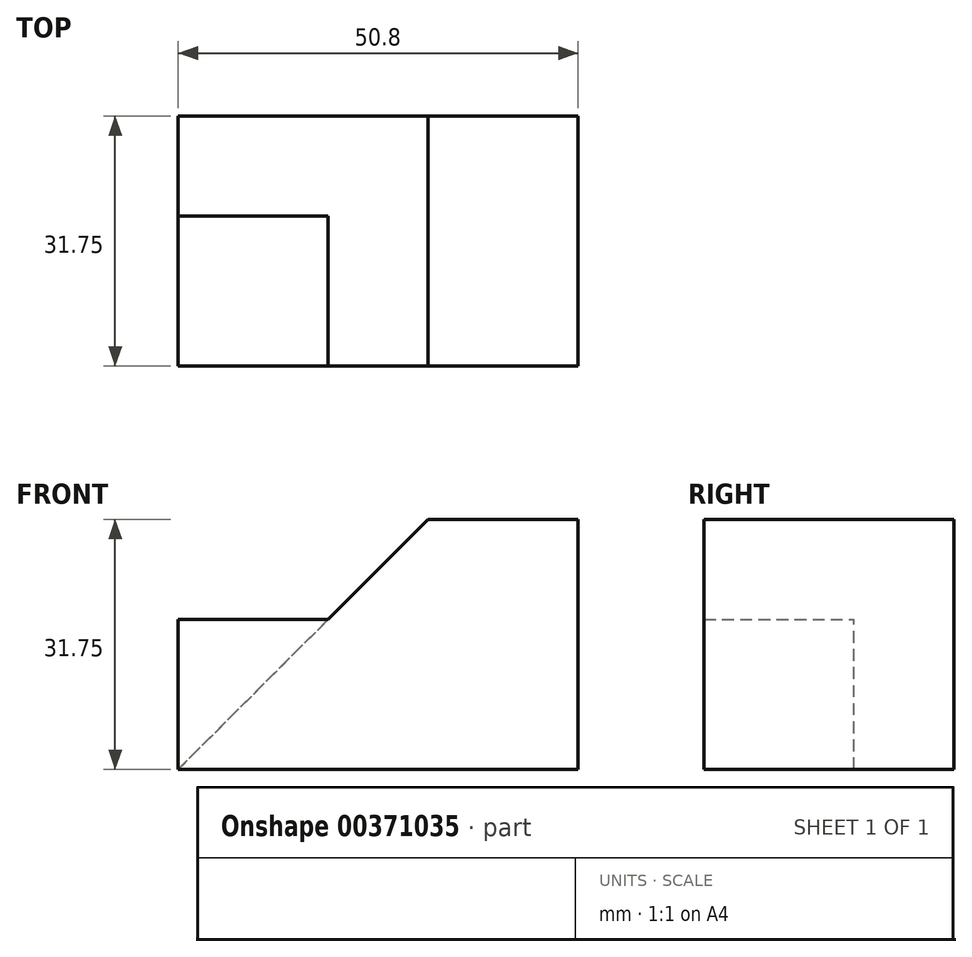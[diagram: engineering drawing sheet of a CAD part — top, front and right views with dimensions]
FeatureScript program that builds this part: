
annotation { "Feature Type Name" : "Feature", "Feature Type Description" : "" }
export const myFeature = defineFeature(function(context is Context, id is Id, definition is map)
    precondition{}
    {
        {
            var Q0;
            Q0=qCreatedBy(makeId("Front.planeOp"),FACE);
            var sketch = newSketch(context, id + "F0", { "sketchPlane" : qUnion([Q0])});
            skLineSegment(sketch, "E0", {"start": v(-48.86, 0) * mm, "end": v(-48.86, 31.75) * mm});
            skLineSegment(sketch, "E1", {"start": v(-48.86, 0) * mm, "end": v(1.94, 0) * mm});
            skLineSegment(sketch, "E2", {"start": v(1.94, 0) * mm, "end": v(1.94, 31.75) * mm});
            skLineSegment(sketch, "E3", {"start": v(-48.86, 31.75) * mm, "end": v(1.94, 31.75) * mm});
            skSolve(sketch);
        }
        {
            var Q0;
            Q0=makeQuery(id+"F0.imprint","IMPRINT",FACE,{"disambiguationData":[TD([[makeQuery(id+"F0.imprint","IMPRINT",EDGE,{"derivedFrom":sQuery(id+"F0.wireOp",EDGE,"E0")}),-1.0]])]});
            extrude(context, id + "F1", {"entities" : qUnion([Q0]), "depth" : 31.75 * mm});
        }
        {
            var Q0;
            Q0=makeQuery(id+"F1.opExtrude","CAP_FACE",FACE,{"disambiguationData":[OSD([sQuery(id+"F0.wireOp",EDGE,"E0"),sQuery(id+"F0.wireOp",EDGE,"E1"),sQuery(id+"F0.wireOp",EDGE,"E2"),sQuery(id+"F0.wireOp",EDGE,"E3")])],"isStart":true});
            var sketch = newSketch(context, id + "F2", { "sketchPlane" : qUnion([Q0])});
            skLineSegment(sketch, "E4", {"start": v(48.86, 0) * mm, "end": v(48.86, 19.05) * mm});
            skLineSegment(sketch, "E5", {"start": v(48.86, 19.05) * mm, "end": v(29.81, 19.05) * mm});
            skLineSegment(sketch, "E6", {"start": v(-1.94, 31.75) * mm, "end": v(17.11, 31.75) * mm});
            skLineSegment(sketch, "E7", {"start": v(17.11, 31.75) * mm, "end": v(29.81, 19.05) * mm});
            skLineSegment(sketch, "E8", {"start": v(17.11, 31.75) * mm, "end": v(48.86, 31.75) * mm});
            skLineSegment(sketch, "E9", {"start": v(48.86, 31.75) * mm, "end": v(48.86, 19.05) * mm});
            skSolve(sketch);
        }
        {
            var Q0;
            Q0=makeQuery(id+"F2.imprint","IMPRINT",FACE,{"disambiguationData":[TD([[makeQuery(id+"F2.imprint","IMPRINT",EDGE,{"derivedFrom":sQuery(id+"F2.wireOp",EDGE,"E5")}),-1.0]])]});
            extrude(context, id + "F3", {"entities" : qUnion([Q0]), "operationType" : NewBodyOperationType.REMOVE, "oppositeDirection" : true, "depth" : 38.1 * mm});
        }
        {
            var Q0;
            Q0=makeQuery(id+"F1.opExtrude","CAP_FACE",FACE,{"disambiguationData":[OSD([sQuery(id+"F0.wireOp",EDGE,"E0"),sQuery(id+"F0.wireOp",EDGE,"E1"),sQuery(id+"F0.wireOp",EDGE,"E2"),sQuery(id+"F0.wireOp",EDGE,"E3")])],"isStart":true});
            var sketch = newSketch(context, id + "F4", { "sketchPlane" : qUnion([Q0])});
            skLineSegment(sketch, "E10", {"start": v(29.81, 19.05) * mm, "end": v(48.86, 0) * mm});
            skSolve(sketch);
        }
        {
            var Q0;
            Q0=makeQuery(id+"F4.imprint","IMPRINT",FACE,{"disambiguationData":[TD([[makeQuery(id+"F4.imprint","IMPRINT",EDGE,{"derivedFrom":sQuery(id+"F4.wireOp",EDGE,"E10")}),1.0]])]});
            var sketch = newSketch(context, id + "F5", { "sketchPlane" : qUnion([Q0])});
            skSolve(sketch);
        }
        {
            var Q0;
            Q0 = qSketchRegion(id + "F5", true);
            var Q1;
            Q1=makeQuery(id+"F4.imprint","IMPRINT",FACE,{"disambiguationData":[TD([[makeQuery(id+"F4.imprint","IMPRINT",EDGE,{"derivedFrom":sQuery(id+"F4.wireOp",EDGE,"E10")}),1.0]])]});
            extrude(context, id + "F6", {"entities" : qUnion([Q0, Q1]), "operationType" : NewBodyOperationType.REMOVE, "oppositeDirection" : true, "depth" : 12.7 * mm});
        }
    });
